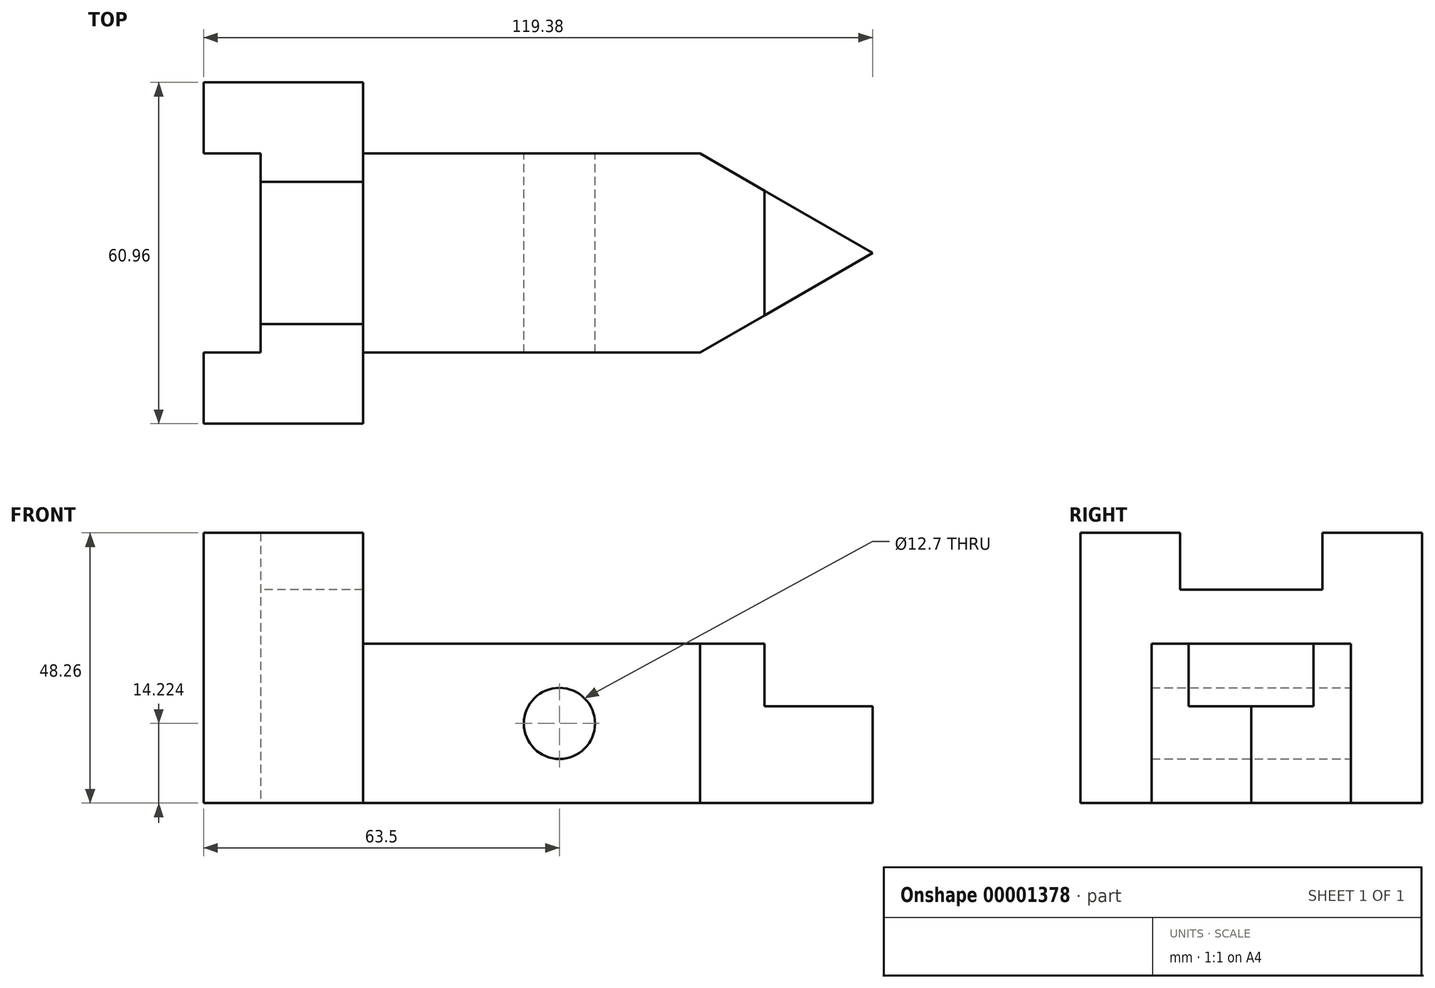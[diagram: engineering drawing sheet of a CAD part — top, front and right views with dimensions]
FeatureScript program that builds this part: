
annotation { "Feature Type Name" : "Feature", "Feature Type Description" : "" }
export const myFeature = defineFeature(function(context is Context, id is Id, definition is map)
    precondition{}
    {
        {
            var Q0;
            Q0=qCreatedBy(makeId("Top.planeOp"),FACE);
            var sketch = newSketch(context, id + "F0", { "sketchPlane" : qUnion([Q0])});
            skLineSegment(sketch, "E0", {"start": v(0, 30.48) * mm, "end": v(0, -30.48) * mm});
            skLineSegment(sketch, "E1", {"start": v(0, -30.48) * mm, "end": v(28.45, -30.48) * mm});
            skLineSegment(sketch, "E2", {"start": v(28.45, -30.48) * mm, "end": v(28.45, 30.48) * mm});
            skLineSegment(sketch, "E3", {"start": v(28.45, 30.48) * mm, "end": v(0, 30.48) * mm});
            skSolve(sketch);
        }
        {
            var Q0;
            Q0=makeQuery(id+"F0.imprint","IMPRINT",FACE,{"disambiguationData":[TD([[makeQuery(id+"F0.imprint","IMPRINT",EDGE,{"derivedFrom":sQuery(id+"F0.wireOp",EDGE,"E0")}),1.0]])]});
            extrude(context, id + "F1", {"entities" : qUnion([Q0]), "depth" : 48.26 * mm});
        }
        {
            var Q0;
            Q0=qCreatedBy(makeId("Top.planeOp"),FACE);
            var sketch = newSketch(context, id + "F2", { "sketchPlane" : qUnion([Q0])});
            skLineSegment(sketch, "E4", {"start": v(28.45, 0) * mm, "end": v(119.38, 0) * mm, "construction": true});
            skLineSegment(sketch, "E5", {"start": v(119.38, 0) * mm, "end": v(88.58, -17.78) * mm});
            skLineSegment(sketch, "E6", {"start": v(88.58, -17.78) * mm, "end": v(28.45, -17.78) * mm});
            skLineSegment(sketch, "E7", {"start": v(28.45, 0) * mm, "end": v(28.45, -17.78) * mm});
            skLineSegment(sketch, "E8.0.MirrorCS", {"start": v(28.45, 0) * mm, "end": v(28.45, 17.78) * mm});
            skLineSegment(sketch, "E8.1.MirrorCS", {"start": v(119.38, 0) * mm, "end": v(88.58, 17.78) * mm});
            skLineSegment(sketch, "E8.2.MirrorCS", {"start": v(88.58, 17.78) * mm, "end": v(28.45, 17.78) * mm});
            skSolve(sketch);
        }
        {
            var Q0;
            Q0 = qSketchRegion(id + "F2", true);
            extrude(context, id + "F3", {"entities" : qUnion([Q0]), "operationType" : NewBodyOperationType.ADD, "depth" : 28.45 * mm});
        }
        {
            var Q0;
            Q0=qCreatedBy(makeId("Front.planeOp"),FACE);
            var sketch = newSketch(context, id + "F4", { "sketchPlane" : qUnion([Q0])});
            skLineSegment(sketch, "E9.bottom", {"start": v(119.38, 28.45) * mm, "end": v(100.08, 28.45) * mm});
            skLineSegment(sketch, "E9.top", {"start": v(119.38, 17.27) * mm, "end": v(100.08, 17.27) * mm});
            skLineSegment(sketch, "E9.left", {"start": v(119.38, 28.45) * mm, "end": v(119.38, 17.27) * mm});
            skLineSegment(sketch, "E9.right", {"start": v(100.08, 28.45) * mm, "end": v(100.08, 17.27) * mm});
            skCircle(sketch, "E10", {"center": v(63.5, 14.22) * mm, "radius": 6.35 * mm});
            skSolve(sketch);
        }
        {
            var Q0;
            {Q0=qUnion([makeQuery(id+"F4.imprint","IMPRINT",FACE,{"disambiguationData":[TD([[makeQuery(id+"F4.imprint","IMPRINT",EDGE,{"derivedFrom":sQuery(id+"F4.wireOp",EDGE,"E9.bottom")}),1.0]])]}),makeQuery(id+"F4.imprint","IMPRINT",FACE,{"disambiguationData":[TD([[makeQuery(id+"F4.imprint","IMPRINT",EDGE,{"derivedFrom":sQuery(id+"F4.wireOp",EDGE,"E10")}),1.0]])]})]);}
            extrude(context, id + "F5", {"entities" : qUnion([Q0]), "operationType" : NewBodyOperationType.REMOVE, "endBound" : BoundingType.THROUGH_ALL, "depth" : 25.4 * mm});
        }
        {
            var Q0;
            Q0=makeQuery(id+"F5.boolean.opBoolean","COPY",FACE,{"derivedFrom":makeQuery(id+"F5.opExtrude","CAP_FACE",FACE,{"disambiguationData":[OSD([sQuery(id+"F4.wireOp",EDGE,"E10")])],"isStart":true})});
            var Q1;
            Q1=makeQuery(id+"F5.boolean.opBoolean","COPY",FACE,{"derivedFrom":makeQuery(id+"F5.opExtrude","CAP_FACE",FACE,{"disambiguationData":[OSD([sQuery(id+"F4.wireOp",EDGE,"E9.bottom"),sQuery(id+"F4.wireOp",EDGE,"E9.top"),sQuery(id+"F4.wireOp",EDGE,"E9.left"),sQuery(id+"F4.wireOp",EDGE,"E9.right")])],"isStart":true})});
            extrude(context, id + "F6", {"entities" : qUnion([Q0, Q1]), "operationType" : NewBodyOperationType.REMOVE, "endBound" : BoundingType.THROUGH_ALL, "oppositeDirection" : true, "depth" : 25.4 * mm});
        }
        {
            var Q0;
            Q0=qCreatedBy(makeId("Top.planeOp"),FACE);
            var sketch = newSketch(context, id + "F7", { "sketchPlane" : qUnion([Q0])});
            skLineSegment(sketch, "E11", {"start": v(0, 17.78) * mm, "end": v(0, -17.78) * mm});
            skLineSegment(sketch, "E12", {"start": v(0, -17.78) * mm, "end": v(10.16, -17.78) * mm});
            skLineSegment(sketch, "E13", {"start": v(10.16, -17.78) * mm, "end": v(10.16, 17.78) * mm});
            skLineSegment(sketch, "E14", {"start": v(10.16, 17.78) * mm, "end": v(0, 17.78) * mm});
            skSolve(sketch);
        }
        {
            var Q0;
            Q0=makeQuery(id+"F7.imprint","IMPRINT",FACE,{"disambiguationData":[TD([[makeQuery(id+"F7.imprint","IMPRINT",EDGE,{"derivedFrom":sQuery(id+"F7.wireOp",EDGE,"E11")}),1.0]])]});
            extrude(context, id + "F8", {"entities" : qUnion([Q0]), "operationType" : NewBodyOperationType.REMOVE, "endBound" : BoundingType.THROUGH_ALL, "depth" : 25.4 * mm});
        }
        {
            var Q0;
            Q0=qCreatedBy(makeId("Right.planeOp"),FACE);
            var sketch = newSketch(context, id + "F9", { "sketchPlane" : qUnion([Q0])});
            skLineSegment(sketch, "E15.rect.bottom", {"start": v(12.7, 48.26) * mm, "end": v(-12.7, 48.26) * mm});
            skLineSegment(sketch, "E15.rect.top", {"start": v(12.7, 38.1) * mm, "end": v(-12.7, 38.1) * mm});
            skLineSegment(sketch, "E15.rect.left", {"start": v(12.7, 48.26) * mm, "end": v(12.7, 38.1) * mm});
            skLineSegment(sketch, "E15.rect.right", {"start": v(-12.7, 48.26) * mm, "end": v(-12.7, 38.1) * mm});
            skPoint(sketch, "E15.rect.middle", {"position": v(0, 43.18) * mm});
            skSolve(sketch);
        }
        {
            var Q0;
            Q0=makeQuery(id+"F9.imprint","IMPRINT",FACE,{"disambiguationData":[TD([[makeQuery(id+"F9.imprint","IMPRINT",EDGE,{"derivedFrom":sQuery(id+"F9.wireOp",EDGE,"E15.rect.bottom")}),1.0]])]});
            extrude(context, id + "F10", {"entities" : qUnion([Q0]), "operationType" : NewBodyOperationType.REMOVE, "endBound" : BoundingType.THROUGH_ALL, "depth" : 25.4 * mm});
        }
    });
